FCSTD DOCUMENT  (FreeCAD 0.19R24366 (Git))
Label: Pi and controller board V1 prototype PCB base
License: All rights reserved
LicenseURL: http://en.wikipedia.org/wiki/All_rights_reserved
objects: Sketcher::SketchObject×1, PartDesign::Body×1
note: 2 computed .brp shape members not serialized (recipe doc carries the construction recipe); baked Part::Feature solids carry a one-line shape summary decoded from their .brp

FEATURE [Sketcher::SketchObject] Sketch
  FullyConstrained = true
  MapMode = 5
  Support = -> [XY_Plane]
  sketch-geometry (50):
    g0: LineSegment StartX=-274.5 StartY=57.336 StartZ=0 EndX=79.5 EndY=57.336 EndZ=0
    g1: LineSegment StartX=82.5 StartY=54.336 StartZ=0 EndX=82.5 EndY=-33.5 EndZ=0
    g2: LineSegment StartX=-277.5 StartY=-33.5 StartZ=0 EndX=-277.5 EndY=54.336 EndZ=0
    g3: ArcOfCircle CenterX=-274.5 CenterY=54.336 CenterZ=0 NormalX=0 NormalY=0 NormalZ=1 AngleXU=0 Radius=3 StartAngle=1.5708 EndAngle=3.14159
    g4: ArcOfCircle CenterX=79.5 CenterY=54.336 CenterZ=0 NormalX=0 NormalY=0 NormalZ=1 AngleXU=0 Radius=3 StartAngle=-5.53353e-11 EndAngle=1.5708
    g5: Circle CenterX=49 CenterY=29 CenterZ=0 NormalX=0 NormalY=0 NormalZ=1 AngleXU=0 Radius=1.35
    g6: Circle CenterX=0 CenterY=29 CenterZ=0 NormalX=0 NormalY=0 NormalZ=1 AngleXU=0 Radius=1.35
    g7: Circle CenterX=49 CenterY=-29 CenterZ=0 NormalX=0 NormalY=0 NormalZ=1 AngleXU=0 Radius=1.35
    g8: Circle CenterX=0 CenterY=-29 CenterZ=0 NormalX=0 NormalY=0 NormalZ=1 AngleXU=0 Radius=1.35
    g9: LineSegment StartX=0 StartY=29 StartZ=0 EndX=49 EndY=29 EndZ=0
    g10: LineSegment StartX=49 StartY=29 StartZ=0 EndX=49 EndY=-29 EndZ=0
    g11: LineSegment StartX=49 StartY=-29 StartZ=0 EndX=0 EndY=-29 EndZ=0
    g12: LineSegment StartX=0 StartY=-29 StartZ=0 EndX=0 EndY=29 EndZ=0
    g13: Circle CenterX=-7.874 CenterY=51.01 CenterZ=0 NormalX=0 NormalY=0 NormalZ=1 AngleXU=0 Radius=1.75
    g14: Circle CenterX=-7.874 CenterY=36.532 CenterZ=0 NormalX=0 NormalY=0 NormalZ=1 AngleXU=0 Radius=1.75
    g15: Circle CenterX=-119.634 CenterY=31.706 CenterZ=0 NormalX=0 NormalY=0 NormalZ=1 AngleXU=0 Radius=1.75
    g16: Circle CenterX=-89.916 CenterY=0.464 CenterZ=0 NormalX=0 NormalY=0 NormalZ=1 AngleXU=0 Radius=1.75
    g17: Circle CenterX=-173.482 CenterY=51.01 CenterZ=0 NormalX=0 NormalY=0 NormalZ=1 AngleXU=0 Radius=1.75
    g18: Circle CenterX=-173.482 CenterY=-27.73 CenterZ=0 NormalX=0 NormalY=0 NormalZ=1 AngleXU=0 Radius=1.75
    g19: LineSegment StartX=-173.482 StartY=51.01 StartZ=0 EndX=-173.482 EndY=-27.73 EndZ=0
    g20: LineSegment StartX=-7.874 StartY=51.01 StartZ=0 EndX=-7.874 EndY=36.532 EndZ=0
    g21: GeomPoint X=0 Y=0 Z=0
    g22: LineSegment StartX=-181.356 StartY=55.836 StartZ=0 EndX=-3.048 EndY=55.836 EndZ=0
    g23: LineSegment StartX=-3.048 StartY=55.836 StartZ=0 EndX=-3.048 EndY=25.864 EndZ=0
    g24: LineSegment StartX=-3.048 StartY=-32.556 StartZ=0 EndX=-181.356 EndY=-32.556 EndZ=0
    g25: LineSegment StartX=-181.356 StartY=-32.556 StartZ=0 EndX=-181.356 EndY=55.836 EndZ=0
    g26: LineSegment StartX=-3.5 StartY=52.5 StartZ=0 EndX=52.5 EndY=52.5 EndZ=0
    g27: LineSegment StartX=52.5 StartY=52.5 StartZ=0 EndX=52.5 EndY=-32.5 EndZ=0
    g28: LineSegment StartX=52.5 StartY=-32.5 StartZ=0 EndX=-3.5 EndY=-32.5 EndZ=0
    g29: LineSegment StartX=-3.5 StartY=-32.5 StartZ=0 EndX=-3.5 EndY=52.5 EndZ=0
    g30: GeomPoint X=24.5 Y=-29 Z=0
    g31: GeomPoint X=24.5 Y=-32.5 Z=0
    g32: LineSegment StartX=24.5 StartY=-29 StartZ=0 EndX=24.5 EndY=-32.5 EndZ=0
    g33: LineSegment StartX=-277.5 StartY=-33.5 StartZ=0 EndX=82.5 EndY=-33.5 EndZ=0
    g34: Circle CenterX=-267.5 CenterY=47.336 CenterZ=0 NormalX=0 NormalY=0 NormalZ=1 AngleXU=0 Radius=2.75
    g35: Circle CenterX=-267.5 CenterY=-23.5 CenterZ=0 NormalX=0 NormalY=0 NormalZ=1 AngleXU=0 Radius=2.75
    g36: Circle CenterX=72.5 CenterY=47.336 CenterZ=0 NormalX=0 NormalY=0 NormalZ=1 AngleXU=0 Radius=2.75
    g37: Circle CenterX=72.5 CenterY=-23.5 CenterZ=0 NormalX=0 NormalY=0 NormalZ=1 AngleXU=0 Radius=2.75
    g38: LineSegment StartX=-267.5 StartY=47.336 StartZ=0 EndX=-267.5 EndY=57.336 EndZ=0
    g39: LineSegment StartX=-267.5 StartY=47.336 StartZ=0 EndX=-267.5 EndY=-23.5 EndZ=0
    g40: LineSegment StartX=-267.5 StartY=-23.5 StartZ=0 EndX=-267.5 EndY=-33.5 EndZ=0
    g41: LineSegment StartX=72.5 StartY=47.336 StartZ=0 EndX=72.5 EndY=57.336 EndZ=0
    g42: LineSegment StartX=72.5 StartY=47.336 StartZ=0 EndX=72.5 EndY=-23.5 EndZ=0
    g43: LineSegment StartX=72.5 StartY=-23.5 StartZ=0 EndX=72.5 EndY=-33.5 EndZ=0
    g44: GeomPoint X=-93.472 Y=-33.5 Z=0
    g45: LineSegment StartX=-3.048 StartY=-25.952 StartZ=0 EndX=2.794 EndY=-25.952 EndZ=0
    g46: LineSegment StartX=2.794 StartY=-25.952 StartZ=0 EndX=2.794 EndY=25.864 EndZ=0
    g47: LineSegment StartX=2.794 StartY=25.864 StartZ=0 EndX=-3.048 EndY=25.864 EndZ=0
    g48: LineSegment StartX=-3.048 StartY=-25.952 StartZ=0 EndX=-3.048 EndY=-32.556 EndZ=0
    g49: LineSegment StartX=-3.048 StartY=25.864 StartZ=0 EndX=-3.048 EndY=-25.952 EndZ=0
  constraints (132):
    c: Vertical(g1)
    c: Tangent(g0,g3) = 1.5708
    c: Tangent(g2,g3) = 1.5708
    c: Tangent(g0,g4) = 1.5708
    c: Tangent(g1,g4) = 1.5708
    c: Coincident(g9,g6)
    c: Coincident(g9,g5)
    c: Horizontal(g9)
    c: Coincident(g10,g5)
    c: Coincident(g10,g7)
    c: Coincident(g11,g7)
    c: Coincident(g11,g8)
    c: Horizontal(g11)
    c: Coincident(g12,g8)
    c: Coincident(g12,g6)
    c: Vertical(g12)
    c: Vertical(g10)
    c: Equal(g6,g5)
    c: Equal(g5,g7)
    c: Equal(g7,g8)
    c: Diameter(g5) = 2.7
    c: DistanceX(g11,g11) = 49
    c: DistanceY(g10,g10) = 58
    c: Coincident(g19,g17)
    c: Coincident(g19,g18)
    c: Coincident(g20,g13)
    c: Coincident(g20,g14)
    c: Vertical(g19)
    c: Vertical(g20)
    c: Equal(g17,g13)
    c: Equal(g13,g14)
    c: Equal(g14,g16)
    c: Equal(g16,g15)
    c: Equal(g15,g18)
    c: Diameter(g17) = 3.5
    c: Radius(g3) = 3
    c: Symmetric(g8,g6,g21)
    c: DistanceX(g14,g21) = 7.874
    c: DistanceY(g21,g14) = 36.532
    c: DistanceY(g21,g13) = 51.01
    c: DistanceY(g21,g16) = 0.464
    c: DistanceX(g16,g21) = 89.916
    c: DistanceY(g21,g15) = 31.706
    c: DistanceX(g15,g21) = 119.634
    c: DistanceX(g18,g21) = 173.482
    c: DistanceY(g18,g21) = 27.73
    c: DistanceY(g21,g17) = 51.01
    c: Horizontal(g0)
    c: Coincident(g22,g23)
    c: Coincident(g48,g24)
    c: Coincident(g24,g25)
    c: Coincident(g25,g22)
    c: Horizontal(g22)
    c: Horizontal(g24)
    c: Vertical(g23)
    c: Vertical(g25)
    c: Coincident(g26,g27)
    c: Coincident(g27,g28)
    c: Coincident(g28,g29)
    c: Coincident(g29,g26)
    c: Horizontal(g26)
    c: Horizontal(g28)
    c: Vertical(g27)
    c: Vertical(g29)
    c: DistanceX(g28,g28) = 56
    c: Coincident(g32,g30)
    c: Coincident(g32,g31)
    c: Vertical(g32)
    c: Symmetric(g8,g7,g32)
    c: Symmetric(g28,g27,g32)
    c: DistanceY(g32,g32) = 3.5
    c: DistanceY(g27,g27) = 85
    c: DistanceX(g24,g24) = 178.308
    c: DistanceY(g21,g22) = 55.836
    c: Horizontal(g33)
    c: Vertical(g2)
    c: DistanceY(g24,g-1) = 32.556
    c: Coincident(g21,g-1)
    c: DistanceX(g24,g27) = 233.856
    c: DistanceX(g2,g1) = 360
    c: Coincident(g33,g1)
    c: Coincident(g33,g2)
    c: Equal(g3,g4)
    c: Equal(g34,g35)
    c: Equal(g35,g37)
    c: Equal(g37,g36)
    c: Diameter(g34) = 5.5
    c: Coincident(g38,g34)
    c: PointOnObject(g38,g0)
    c: Vertical(g38)
    c: Coincident(g39,g34)
    c: Coincident(g39,g35)
    c: Vertical(g39)
    c: Coincident(g40,g35)
    c: PointOnObject(g40,g33)
    c: Vertical(g40)
    c: Coincident(g41,g36)
    c: PointOnObject(g41,g0)
    c: Vertical(g41)
    c: Coincident(g42,g36)
    c: Coincident(g42,g37)
    c: Vertical(g42)
    c: Coincident(g43,g37)
    c: PointOnObject(g43,g33)
    c: Vertical(g43)
    c: Equal(g43,g41)
    c: Equal(g41,g40)
    c: Equal(g40,g38)
    c: DistanceY(g40,g40) = 10
    c: DistanceX(g2,g40) = 10
    c: DistanceX(g43,g1) = 10
    c: DistanceX(g27,g43) = 20
    c: DistanceY(g1,g27) = 1
    c: PointOnObject(g44,g33)
    c: DistanceX(g44,g-1) = 93.472
    c: DistanceX(g44,g27) = 145.972
    c: DistanceX(g48,g-1) = 3.048
    c: Horizontal(g45)
    c: Coincident(g46,g45)
    c: Vertical(g46)
    c: Coincident(g47,g46)
    c: Horizontal(g47)
    c: DistanceX(g-1,g46) = 2.794
    c: DistanceY(g45,g-1) = 25.952
    c: DistanceY(g-1,g46) = 25.864
    c: Coincident(g23,g47)
    c: Coincident(g48,g45)
    c: Tangent(g23,g48)
    c: Coincident(g49,g47)
    c: Coincident(g49,g45)
    c: DistanceY(g46,g46) = 51.816
    c: DistanceY(g22,g0) = 1.5
FEATURE [PartDesign::Body] Body
  Group = -> [Sketch]
  Origin = -> Origin
